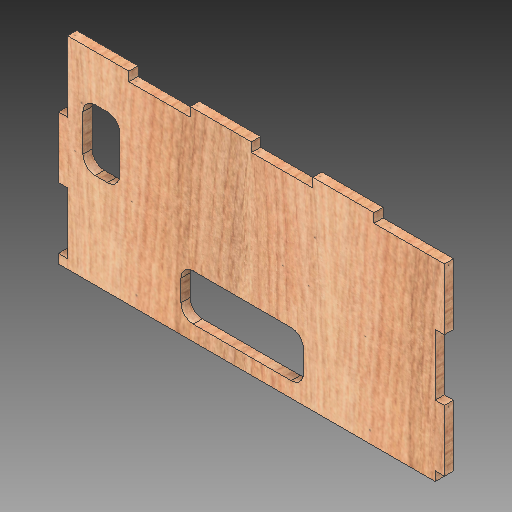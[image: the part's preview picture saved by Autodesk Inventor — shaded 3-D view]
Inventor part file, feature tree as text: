
AUTODESK INVENTOR PART (.ipt)
format: ipt  version: 2018.2 (Build 222227000, 227)  size: 381,440 bytes
history: native  units: mm
features: extrude x2, sketch x2, fillet x1
ambient origin geometry x8: Origin, YZ Plane, XZ Plane, XY Plane, X Axis, Y Axis, Z Axis, Center Point
bodies: Solid1 (feature_tree)
feature tree (5):
  extrude  "Extrusion1"  Depth=120.0mm
  extrude  "Extrusion2"  Depth=20.0mm
  fillet  "Fillet1"  Radius=20.0mm
  sketch  "Sketch1"  dims[d0=3.0mm d1=120.0mm]
  sketch  "Sketch2"  dims[d2=3.0mm d3=20.0mm d4=20.0mm d5=20.0mm d6=3.0mm d7=20.0mm d8=20.0mm d9=20.0mm d10=20.0mm d11=20.0mm d12=20.0mm d13=3.0mm d14=20.0mm d15=20.0mm d16=20.0mm d17=3.0mm d18=0.0mm d19=40.0mm d20=15.0mm d21=5.0mm d22=40.0mm d23=10.0mm d24=0.0mm d26=12.0mm d27=20.0mm d28=12.0mm d29=5.0mm d30=4.0mm]
